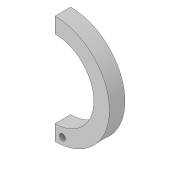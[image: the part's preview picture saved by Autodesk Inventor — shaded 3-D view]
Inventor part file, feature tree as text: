
AUTODESK INVENTOR PART (.ipt)
format: ipt  version: 2019 (Build 230136000, 136)  size: 92,672 bytes
history: native  units: in
note: dims shown in document units (in); Inventor stores cm internally (conversion verified against a paired STEP export)
features: extrude x3, sketch x3
ambient origin geometry x8: Origin, YZ Plane, XZ Plane, XY Plane, X Axis, Y Axis, Z Axis, Center Point
bodies: Solid1 (feature_tree)
feature tree (6):
  extrude  "Extrusion1"  Depth=0.3937in TaperAngle=0.0deg
  extrude  "Extrusion2"  Depth=0.1575in
  extrude  "Extrusion3"  Depth=0.3937in TaperAngle=0.0deg
  sketch  "Sketch1"  dims[d0=2.7559in d1=0.3937in d2=0.0in]
  sketch  "Sketch2"  dims[d3=1.9685in d4=0.1575in]
  sketch  "Sketch3"  dims[d5=0.3937in d6=0.0in d7=0.3937in d8=0.0in]
